FCSTD DOCUMENT  (FreeCAD 0.20R29603 (Git))
Label: pcb-outline
License: All rights reserved
LicenseURL: http://en.wikipedia.org/wiki/All_rights_reserved
objects: Sketcher::SketchObject×1
note: 1 computed .brp shape members not serialized (recipe doc carries the construction recipe); baked Part::Feature solids carry a one-line shape summary decoded from their .brp

FEATURE [Sketcher::SketchObject] Sketch
  FullyConstrained = true
  sketch-geometry (8):
    g0: ArcOfCircle CenterX=0 CenterY=0 CenterZ=0 NormalX=0 NormalY=0 NormalZ=1 AngleXU=0 Radius=43 StartAngle=2.54055 EndAngle=8.28049
    g1: LineSegment StartX=-32.2825 StartY=24.4712 StartZ=0 EndX=-25.2118 EndY=16.0448 EndZ=0
    g2: LineSegment StartX=-11.6695 StartY=24.7973 StartZ=0 EndX=-22.3941 EndY=15.7982 EndZ=0
    g3: LineSegment StartX=-11.423 StartY=27.6149 StartZ=0 EndX=-18.4937 EndY=36.0414 EndZ=0
    g4: ArcOfCircle CenterX=-23.6797 CenterY=17.3303 CenterZ=0 NormalX=0 NormalY=0 NormalZ=1 AngleXU=0 Radius=2 StartAngle=3.83972 EndAngle=5.41052
    g5: ArcOfCircle CenterX=-12.9551 CenterY=26.3294 CenterZ=0 NormalX=0 NormalY=0 NormalZ=1 AngleXU=0 Radius=2 StartAngle=5.41052 EndAngle=6.98132
    g6: ArcOfCircle CenterX=-16.9616 CenterY=37.327 CenterZ=0 NormalX=0 NormalY=0 NormalZ=1 AngleXU=0 Radius=2 StartAngle=1.99731 EndAngle=3.83972
    g7: ArcOfCircle CenterX=-33.8146 CenterY=23.1857 CenterZ=0 NormalX=0 NormalY=0 NormalZ=1 AngleXU=0 Radius=2 StartAngle=0.698132 EndAngle=2.54055
  constraints (20):
    c: Coincident(g0,g-1)
    c: Tangent(g1,g4) = -1.5708
    c: Tangent(g2,g4) = 1.5708
    c: Tangent(g2,g5) = 1.5708
    c: Tangent(g3,g5) = -1.5708
    c: Tangent(g0,g6) = -1.5708
    c: Tangent(g3,g6) = 1.5708
    c: Tangent(g1,g7) = 1.5708
    c: Tangent(g0,g7) = -1.5708
    c: Radius(g0) = 43
    c: Radius(g6) = 2
    c: Equal(g6,g7)
    c: Equal(g7,g4)
    c: Equal(g4,g5)
    c: Equal(g1,g3)
    c: Parallel(g1,g3)
    c: Perpendicular(g2,g3)
    c: Distance(g1) = 11
    c: Distance(g2) = 14
    c: Angle(g3) = 2.26893
